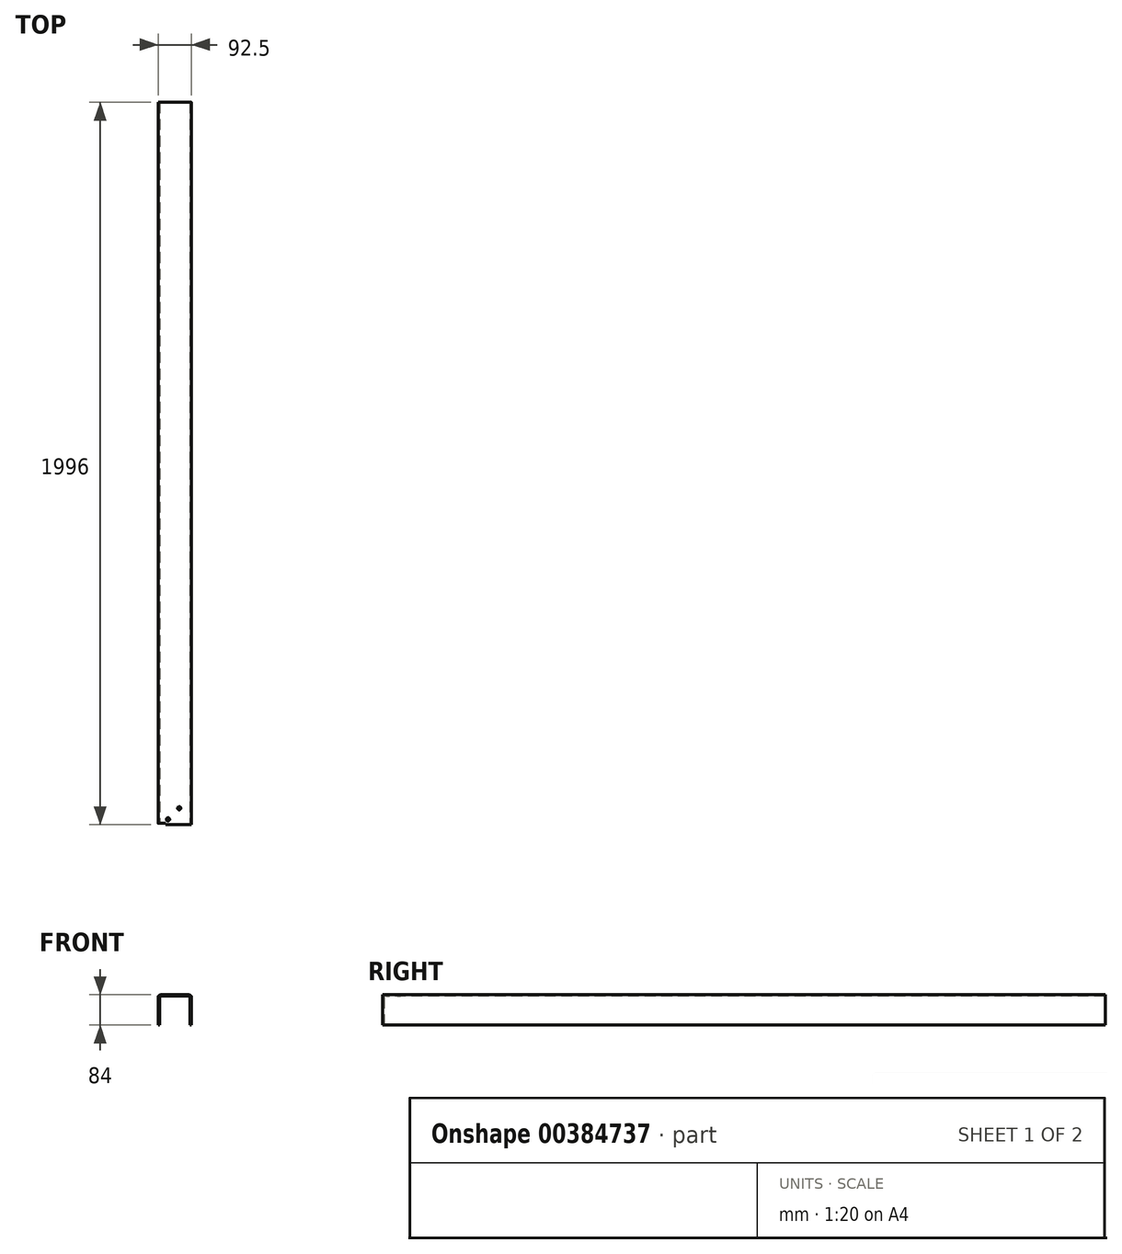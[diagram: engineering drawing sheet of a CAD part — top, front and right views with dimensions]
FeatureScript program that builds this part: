
annotation { "Feature Type Name" : "Feature", "Feature Type Description" : "" }
export const myFeature = defineFeature(function(context is Context, id is Id, definition is map)
    precondition{}
    {
        {
            var Q0;
            Q0=qCreatedBy(makeId("Front.planeOp"),FACE);
            var sketch = newSketch(context, id + "F0", { "sketchPlane" : qUnion([Q0])});
            skLineSegment(sketch, "E0.bottom", {"start": v(-46.25, -42) * mm, "end": v(-42.25, -42) * mm});
            skLineSegment(sketch, "E0.top", {"start": v(-38.25, 42) * mm, "end": v(38.25, 42) * mm});
            skLineSegment(sketch, "E0.left", {"start": v(-46.25, -42) * mm, "end": v(-46.25, 34) * mm});
            skLineSegment(sketch, "E0.right", {"start": v(46.25, -42) * mm, "end": v(46.25, 34) * mm});
            skPoint(sketch, "E0.middle", {"position": v(0, 0) * mm});
            skLineSegment(sketch, "E1", {"start": v(-42.25, -42) * mm, "end": v(-42.25, 34) * mm});
            skLineSegment(sketch, "E2", {"start": v(-38.25, 38) * mm, "end": v(38.25, 38) * mm});
            skLineSegment(sketch, "E3", {"start": v(42.25, 34) * mm, "end": v(42.25, -42) * mm});
            skLineSegment(sketch, "E4.trimOffspring", {"start": v(42.25, -42) * mm, "end": v(46.25, -42) * mm});
            skPoint(sketch, "E5.visualSharp", {"position": v(-42.25, 38) * mm});
            skArc(sketch, "E5.filletArc", {"start": v(-38.25, 38) * mm, "mid": v(-41.08, 36.83) * mm, "end": v(-42.25, 34) * mm});
            skPoint(sketch, "E6.visualSharp", {"position": v(42.25, 38) * mm});
            skArc(sketch, "E6.filletArc", {"start": v(42.25, 34) * mm, "mid": v(41.08, 36.83) * mm, "end": v(38.25, 38) * mm});
            skPoint(sketch, "E7.visualSharp", {"position": v(-46.25, 42) * mm});
            skArc(sketch, "E7.filletArc", {"start": v(-38.25, 42) * mm, "mid": v(-43.9, 39.66) * mm, "end": v(-46.25, 34) * mm});
            skPoint(sketch, "E8.visualSharp", {"position": v(46.25, 42) * mm});
            skArc(sketch, "E8.filletArc", {"start": v(46.25, 34) * mm, "mid": v(43.9, 39.66) * mm, "end": v(38.25, 42) * mm});
            skSolve(sketch);
        }
        {
            var Q0;
            Q0=makeQuery(id+"F0.imprint","IMPRINT",FACE,{"disambiguationData":[TD([[makeQuery(id+"F0.imprint","IMPRINT",EDGE,{"derivedFrom":sQuery(id+"F0.wireOp",EDGE,"E0.bottom")}),1.0]])]});
            extrude(context, id + "F1", {"entities" : qUnion([Q0]), "oppositeDirection" : true, "depth" : 1996 * mm});
        }
        {
            var Q0;
            Q0=qCreatedBy(makeId("Right.planeOp"),FACE);
            var Q1;
            Q1=makeQuery(id+"F1.opExtrude","CAP_EDGE",EDGE,{"disambiguationData":[OSD([sQuery(id+"F0.wireOp",EDGE,"E0.left")])],"isStart":true});
            cPlane(context, id + "F2", {"entities" : qUnion([Q0, Q1]), "cplaneType" : CPlaneType.LINE_ANGLE, "offset" : 25 * mm, "angle" : 0 * degree, "width" : 150 * mm, "height" : 150 * mm});
        }
        {
            var Q0;
            Q0=qCreatedBy(id+"F2.planeOp",FACE);
            var sketch = newSketch(context, id + "F3", { "sketchPlane" : qUnion([Q0])});
            skLineSegment(sketch, "E9.bottom", {"start": v(0, -43.13) * mm, "end": v(-4, -43.13) * mm});
            skLineSegment(sketch, "E9.top", {"start": v(0, 43.87) * mm, "end": v(-4, 43.87) * mm});
            skLineSegment(sketch, "E9.left", {"start": v(0, -43.13) * mm, "end": v(0, 43.87) * mm});
            skLineSegment(sketch, "E9.right", {"start": v(-4, -43.13) * mm, "end": v(-4, 43.87) * mm});
            skSolve(sketch);
        }
        {
            var Q0;
            Q0=makeQuery(id+"F3.imprint","IMPRINT",FACE,{"disambiguationData":[TD([[makeQuery(id+"F3.imprint","IMPRINT",EDGE,{"derivedFrom":sQuery(id+"F3.wireOp",EDGE,"E9.bottom")}),-1.0]])]});
            extrude(context, id + "F4", {"entities" : qUnion([Q0]), "operationType" : NewBodyOperationType.REMOVE, "oppositeDirection" : true, "depth" : 21.4 * mm});
        }
        {
            var Q0;
            Q0=makeQuery(id+"F1.opExtrude","SWEPT_FACE",FACE,{"disambiguationData":[OSD([sQuery(id+"F0.wireOp",EDGE,"E2")])]});
            var sketch = newSketch(context, id + "F5", { "sketchPlane" : qUnion([Q0])});
            skPoint(sketch, "E10.middle", {"position": v(0, 0) * mm});
            skLineSegment(sketch, "E11", {"start": v(18.92, 0) * mm, "end": v(-18.92, 0) * mm});
            skPoint(sketch, "E10.bottom.end.orphan", {"position": v(-18.92, 14.5) * mm});
            skPoint(sketch, "E10.bottom.start.orphan", {"position": v(18.92, 14.5) * mm});
            skCircle(sketch, "E12", {"center": v(-18.92, -14.5) * mm, "radius": 4.5 * mm});
            skPoint(sketch, "E10.left.end.orphan", {"position": v(18.92, -14.5) * mm});
            skSolve(sketch);
        }
        {
            var Q0;
            {var subQ6=sQuery(id+"F5.wireOp",EDGE,"E11");Q0=makeQuery(id+"F5.imprint","IMPRINT",FACE,{"disambiguationData":[TD([[makeQuery(id+"F5.imprint","IMPRINT",EDGE,{"derivedFrom":subQ6}),-1.0]])]});}
            var sketch = newSketch(context, id + "F6", { "sketchPlane" : qUnion([Q0])});
            skPoint(sketch, "E13.middle", {"position": v(0, 0) * mm});
            skCircle(sketch, "E14", {"center": v(12.06, -45.5) * mm, "radius": 4.5 * mm});
            skPoint(sketch, "E13.right.end.orphan", {"position": v(-12.06, -45.5) * mm});
            skPoint(sketch, "E13.bottom.end.orphan", {"position": v(-12.06, 45.5) * mm});
            skPoint(sketch, "E13.bottom.start.orphan", {"position": v(12.06, 45.5) * mm});
            skSolve(sketch);
        }
        {
            var Q0;
            Q0=makeQuery(id+"F6.imprint","IMPRINT",FACE,{"disambiguationData":[TD([[makeQuery(id+"F6.imprint","IMPRINT",EDGE,{"derivedFrom":sQuery(id+"F6.wireOp",EDGE,"E14")}),1.0]])]});
            var Q1;
            Q1=makeQuery(id+"F5.imprint","IMPRINT",FACE,{"disambiguationData":[TD([[makeQuery(id+"F5.imprint","IMPRINT",EDGE,{"derivedFrom":sQuery(id+"F5.wireOp",EDGE,"E12")}),1.0]])]});
            extrude(context, id + "F7", {"entities" : qUnion([Q0, Q1]), "operationType" : NewBodyOperationType.REMOVE, "oppositeDirection" : true, "depth" : 4 * mm});
        }
    });
